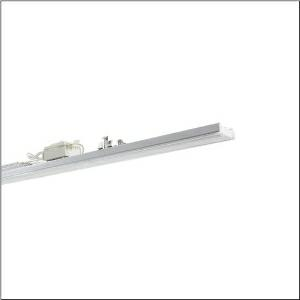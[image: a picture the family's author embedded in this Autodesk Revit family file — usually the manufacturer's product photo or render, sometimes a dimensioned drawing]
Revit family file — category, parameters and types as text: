
# Revit family: licross_11_recessed_ho_51te1wdv465m
name_source: partatom
category: Lighting Fixtures
units: mm (PartAtom-declared; Revit-internal decimal feet)

## family parameters
Cut with Voids When Loaded = No
Host = Face
Light Source = No
Part Type = Normal
Room Calculation Point = No
Round Connector Dimension = Use Diameter
Shared = No

## types (1)
- --- (1 x LED, 6760 lm, 34.7 W, 4000K)
    Apparent Load = 35 VA
    CIE Flux Codes = 73 94 99 100 100
    Color Rendering = 80
    Color Temperature = 4000K
    Default Elevation = 1800 mm
    Description = Licross 11 Recessed HO, luminaire insert, of sheet steel, coil coated, white, length: 2.250mm, width: 66mm, height: 67mm, LED rated luminous flux: 6.760lm, light colour: 840, SDCM (Standard Deviation of Colour Matching)MacAdam ≤ 2 SDCM (initial), control gear: DALI 2, with plug, 5-pole, with phase selection, mains connection: 220..240V, AC, 50/60Hz, rated input power: 35W, internal wiring halogen-free, primary optical cover: cover, of PMMA, light emission: direct distribution, primary light characteristic: symmetric, protection rating (complete): IP54, insulation class (complete): insulation class I (protective earthing), certification: CE, ENEC, VDE, UKCA, protection symbol: D if used in an environment without relevant dust loads with corresponding accessories, impact resistance: IK06, permissible ambient temperature for indoor applications: -25..+40°C, corresponds to IFS (International Featured Standards) requirements for safety and quality in the food industry, reducing of maximum allowable ambient temperature of 5°C with ceiling mounting, LABS conformity tested according to VDMA 24364:2018-05, The light source and the operating device comply with the requirements of the Ecodesign Regulation (EU) 2019/2020 and are replaceable in accordance with this regulation, packaging unit: 1 piece
    Height = 58 mm
    Lamp = 1 x LED
    Lamp Light Flux = 6760 lm
    Lamp Power = 34.7 W
    Lamp count = 1
    Length = 2250 mm
    Luminous efficacy = 195 lm/W
    Manufacturer = Siteco
    ModVariant = No
    Model = 51TE1WDV465M
    Mounting Place = Ceiling
    Mounting Type = Pendant
    Number of Poles = 1
    OnlyDefault = Yes
    Power Factor = 1
    Product Name = Licross 11 Recessed HO
    Product group = luminaire insert | ceiling pendant
    ProductGroupID = 901
    Protection Class = Protection class I
    Protection Degree = IP 54
    RLX_Detail_Level = 1
    RLX_Emergency_Light_Flux = 0 lm
    RLX_Emergency_Type = 0
    RLX_Emergency_Type_DB = No
    RlxData = <blob elided: 29545 chars, md5=a7ad6cdf>
    Socket = socket
    Standby Power = 0 W
    System Light Flux = 6760 lm
    System Power = 35 W
    Type Comments = factory setting: luminous flux: 100 % | dim-lin: 254 | 158 mA
    Type Image = l_1296930.jpg
    URL = http://relux.com
    VarID = @adj_037641
    Voltage = 0 V
    Weight = 0.00 kg
    Width = 66 mm

## geometry (parser evidence)
native form markers: Blend x4, Sweep x10
no freeform markers — native parametric forms only
